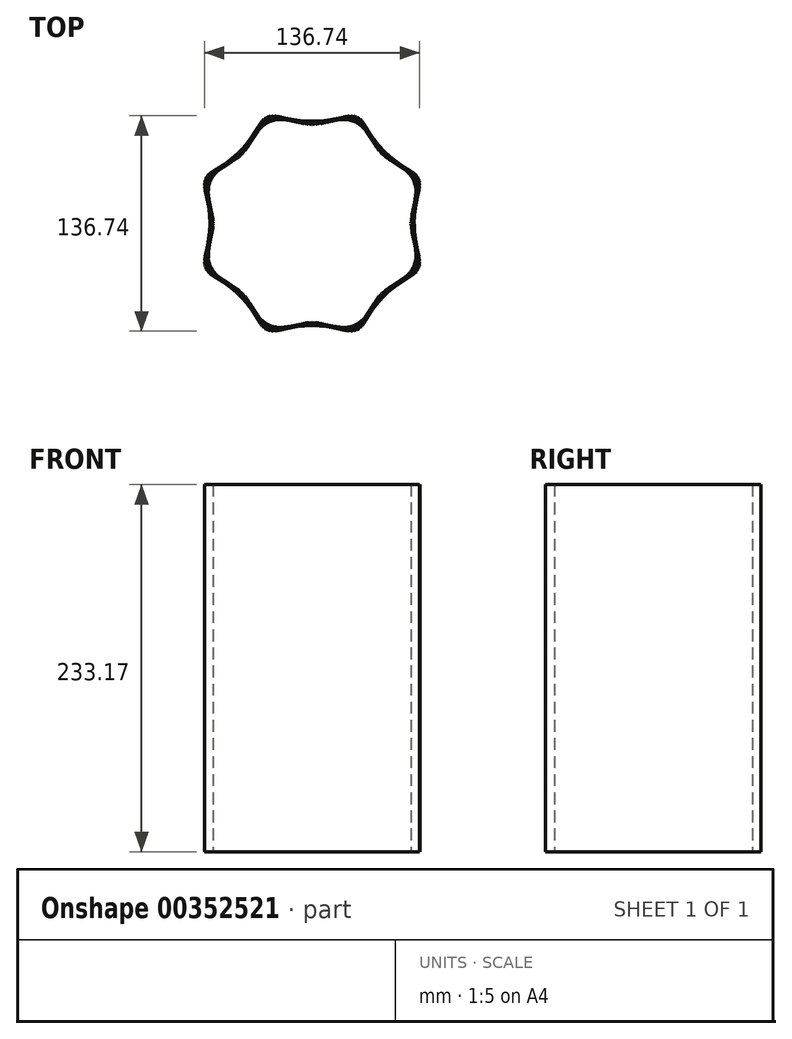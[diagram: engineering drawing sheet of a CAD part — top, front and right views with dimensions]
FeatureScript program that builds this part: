
annotation { "Feature Type Name" : "Feature", "Feature Type Description" : "" }
export const myFeature = defineFeature(function(context is Context, id is Id, definition is map)
    precondition{}
    {
        {
            var Q0;
            Q0=qCreatedBy(makeId("Top.planeOp"),FACE);
            var sketch = newSketch(context, id + "F0", { "sketchPlane" : qUnion([Q0])});
            skLineSegment(sketch, "E0", {"start": v(0, 0) * mm, "end": v(0, 62.86) * mm});
            skLineSegment(sketch, "E1.1.0", {"start": v(0, 0) * mm, "end": v(-44.45, 44.45) * mm});
            skLineSegment(sketch, "E1.2.0", {"start": v(0, 0) * mm, "end": v(-62.86, 0) * mm});
            skLineSegment(sketch, "E1.3.0", {"start": v(0, 0) * mm, "end": v(-44.45, -44.45) * mm});
            skLineSegment(sketch, "E1.4.0", {"start": v(0, 0) * mm, "end": v(0, -62.86) * mm});
            skLineSegment(sketch, "E1.5.0", {"start": v(0, 0) * mm, "end": v(44.45, -44.45) * mm});
            skLineSegment(sketch, "E1.6.0", {"start": v(0, 0) * mm, "end": v(62.86, 0) * mm});
            skLineSegment(sketch, "E1.7.0", {"start": v(0, 0) * mm, "end": v(44.45, 44.45) * mm});
            skPoint(sketch, "E1.center", {"position": v(0, 0) * mm});
            skSolve(sketch);
        }
        {
            var Q0;
            Q0=qCreatedBy(makeId("Top.planeOp"),FACE);
            var sketch = newSketch(context, id + "F1", { "sketchPlane" : qUnion([Q0])});
            skLineSegment(sketch, "E2", {"start": v(0, 0) * mm, "end": v(40.7, 0) * mm});
            skLineSegment(sketch, "E3.1.0", {"start": v(0, 0) * mm, "end": v(37.6, 15.58) * mm});
            skLineSegment(sketch, "E3.2.0", {"start": v(0, 0) * mm, "end": v(28.78, 28.78) * mm});
            skLineSegment(sketch, "E3.3.0", {"start": v(0, 0) * mm, "end": v(15.58, 37.6) * mm});
            skLineSegment(sketch, "E3.4.0", {"start": v(0, 0) * mm, "end": v(0, 40.7) * mm});
            skLineSegment(sketch, "E3.5.0", {"start": v(0, 0) * mm, "end": v(-15.58, 37.6) * mm});
            skLineSegment(sketch, "E3.6.0", {"start": v(0, 0) * mm, "end": v(-28.78, 28.78) * mm});
            skLineSegment(sketch, "E3.7.0", {"start": v(0, 0) * mm, "end": v(-37.6, 15.58) * mm});
            skLineSegment(sketch, "E3.8.0", {"start": v(0, 0) * mm, "end": v(-40.7, 0) * mm});
            skLineSegment(sketch, "E3.9.0", {"start": v(0, 0) * mm, "end": v(-37.6, -15.58) * mm});
            skLineSegment(sketch, "E3.10.0", {"start": v(0, 0) * mm, "end": v(-28.78, -28.78) * mm});
            skLineSegment(sketch, "E3.11.0", {"start": v(0, 0) * mm, "end": v(-15.58, -37.6) * mm});
            skLineSegment(sketch, "E3.12.0", {"start": v(0, 0) * mm, "end": v(0, -40.7) * mm});
            skLineSegment(sketch, "E3.13.0", {"start": v(0, 0) * mm, "end": v(15.58, -37.6) * mm});
            skLineSegment(sketch, "E3.14.0", {"start": v(0, 0) * mm, "end": v(28.78, -28.78) * mm});
            skLineSegment(sketch, "E3.15.0", {"start": v(0, 0) * mm, "end": v(37.6, -15.58) * mm});
            skPoint(sketch, "E3.center", {"position": v(0, 0) * mm});
            skSolve(sketch);
        }
        {
            var Q0;
            Q0=qCreatedBy(makeId("Top.planeOp"),FACE);
            cPlane(context, id + "F2", {"entities" : qUnion([Q0]), "cplaneType" : CPlaneType.OFFSET, "offset" : 110.49 * mm, "oppositeDirection" : true, "width" : 152.4 * mm, "height" : 152.4 * mm});
        }
        {
            var Q0;
            Q0=qCreatedBy(id+"F2.planeOp",FACE);
            var sketch = newSketch(context, id + "F3", { "sketchPlane" : qUnion([Q0])});
            skLineSegment(sketch, "E4", {"start": v(0, 0) * mm, "end": v(0, 62.86) * mm});
            skLineSegment(sketch, "E5.1.0", {"start": v(0, 0) * mm, "end": v(-44.45, 44.45) * mm});
            skLineSegment(sketch, "E5.2.0", {"start": v(0, 0) * mm, "end": v(-62.86, 0) * mm});
            skLineSegment(sketch, "E5.3.0", {"start": v(0, 0) * mm, "end": v(-44.45, -44.45) * mm});
            skLineSegment(sketch, "E5.4.0", {"start": v(0, 0) * mm, "end": v(0, -62.86) * mm});
            skLineSegment(sketch, "E5.5.0", {"start": v(0, 0) * mm, "end": v(44.45, -44.45) * mm});
            skLineSegment(sketch, "E5.6.0", {"start": v(0, 0) * mm, "end": v(62.86, 0) * mm});
            skLineSegment(sketch, "E5.7.0", {"start": v(0, 0) * mm, "end": v(44.45, 44.45) * mm});
            skPoint(sketch, "E5.center", {"position": v(0, 0) * mm});
            skSolve(sketch);
        }
        {
            var Q0;
            Q0=qCreatedBy(id+"F2.planeOp",FACE);
            var sketch = newSketch(context, id + "F4", { "sketchPlane" : qUnion([Q0])});
            skLineSegment(sketch, "E6", {"start": v(0, 0) * mm, "end": v(0, 73.37) * mm});
            skLineSegment(sketch, "E7.1.0", {"start": v(0, 0) * mm, "end": v(-28.08, 67.79) * mm});
            skLineSegment(sketch, "E7.2.0", {"start": v(0, 0) * mm, "end": v(-51.88, 51.88) * mm});
            skLineSegment(sketch, "E7.3.0", {"start": v(0, 0) * mm, "end": v(-67.79, 28.08) * mm});
            skLineSegment(sketch, "E7.4.0", {"start": v(0, 0) * mm, "end": v(-73.37, 0) * mm});
            skLineSegment(sketch, "E7.5.0", {"start": v(0, 0) * mm, "end": v(-67.79, -28.08) * mm});
            skLineSegment(sketch, "E7.6.0", {"start": v(0, 0) * mm, "end": v(-51.88, -51.88) * mm});
            skLineSegment(sketch, "E7.7.0", {"start": v(0, 0) * mm, "end": v(-28.08, -67.79) * mm});
            skLineSegment(sketch, "E7.8.0", {"start": v(0, 0) * mm, "end": v(0, -73.37) * mm});
            skLineSegment(sketch, "E7.9.0", {"start": v(0, 0) * mm, "end": v(28.08, -67.79) * mm});
            skLineSegment(sketch, "E7.10.0", {"start": v(0, 0) * mm, "end": v(51.88, -51.88) * mm});
            skLineSegment(sketch, "E7.11.0", {"start": v(0, 0) * mm, "end": v(67.79, -28.08) * mm});
            skLineSegment(sketch, "E7.12.0", {"start": v(0, 0) * mm, "end": v(73.37, 0) * mm});
            skLineSegment(sketch, "E7.13.0", {"start": v(0, 0) * mm, "end": v(67.79, 28.08) * mm});
            skLineSegment(sketch, "E7.14.0", {"start": v(0, 0) * mm, "end": v(51.88, 51.88) * mm});
            skLineSegment(sketch, "E7.15.0", {"start": v(0, 0) * mm, "end": v(28.08, 67.79) * mm});
            skPoint(sketch, "E7.center", {"position": v(0, 0) * mm});
            skSolve(sketch);
        }
        {
            var Q0;
            Q0=qCreatedBy(id+"F2.planeOp",FACE);
            cPlane(context, id + "F5", {"entities" : qUnion([Q0]), "cplaneType" : CPlaneType.OFFSET, "offset" : 63 * mm, "oppositeDirection" : true, "width" : 152.4 * mm, "height" : 152.4 * mm});
        }
        {
            var Q0;
            Q0=qCreatedBy(id+"F5.planeOp",FACE);
            var sketch = newSketch(context, id + "F6", { "sketchPlane" : qUnion([Q0])});
            skLineSegment(sketch, "E8", {"start": v(0, 0) * mm, "end": v(0, 62.86) * mm});
            skLineSegment(sketch, "E9.1.0", {"start": v(0, 0) * mm, "end": v(-44.45, 44.45) * mm});
            skLineSegment(sketch, "E9.2.0", {"start": v(0, 0) * mm, "end": v(-62.86, 0) * mm});
            skLineSegment(sketch, "E9.3.0", {"start": v(0, 0) * mm, "end": v(-44.45, -44.45) * mm});
            skLineSegment(sketch, "E9.4.0", {"start": v(0, 0) * mm, "end": v(0, -62.86) * mm});
            skLineSegment(sketch, "E9.5.0", {"start": v(0, 0) * mm, "end": v(44.45, -44.45) * mm});
            skLineSegment(sketch, "E9.6.0", {"start": v(0, 0) * mm, "end": v(62.86, 0) * mm});
            skLineSegment(sketch, "E9.7.0", {"start": v(0, 0) * mm, "end": v(44.45, 44.45) * mm});
            skPoint(sketch, "E9.center", {"position": v(0, 0) * mm});
            skFitSpline(sketch, "E10", {"points": [v(0, 62.86) * mm, v(28.08, 67.79) * mm, v(44.46, 44.45) * mm, v(67.8, 28.08) * mm, v(62.87, 0) * mm, v(67.77, -28.07) * mm, v(44.46, -44.45) * mm, v(28.08, -67.8) * mm, v(0, -62.87) * mm, v(-28.07, -67.8) * mm, v(-44.45, -44.45) * mm, v(-67.78, -28.08) * mm, v(-62.86, 0) * mm, v(-67.78, 28.08) * mm, v(-44.45, 44.45) * mm, v(-28.07, 67.79) * mm, v(0, 62.86) * mm]});
            skSolve(sketch);
        }
        {
            var Q0;
            Q0=qCreatedBy(id+"F2.planeOp",FACE);
            cPlane(context, id + "F7", {"entities" : qUnion([Q0]), "cplaneType" : CPlaneType.OFFSET, "offset" : 170.18 * mm, "width" : 152.4 * mm, "height" : 152.4 * mm});
        }
        {
            var Q0;
            Q0=qCreatedBy(id+"F7.planeOp",FACE);
            var sketch = newSketch(context, id + "F8", { "sketchPlane" : qUnion([Q0])});
            skFitSpline(sketch, "E11", {"points": [v(0, 62.86) * mm, v(28.08, 67.79) * mm, v(44.46, 44.45) * mm, v(67.8, 28.08) * mm, v(62.87, 0) * mm, v(67.77, -28.07) * mm, v(44.46, -44.45) * mm, v(28.08, -67.8) * mm, v(0, -62.87) * mm, v(-28.07, -67.8) * mm, v(-44.45, -44.45) * mm, v(-67.78, -28.08) * mm, v(-62.86, 0) * mm, v(-67.78, 28.08) * mm, v(-44.45, 44.45) * mm, v(-28.07, 67.79) * mm, v(0, 62.86) * mm]});
            skLineSegment(sketch, "E12", {"start": v(0, 0) * mm, "end": v(0, 62.86) * mm});
            skLineSegment(sketch, "E13.1.0", {"start": v(0, 0) * mm, "end": v(-44.45, 44.45) * mm});
            skLineSegment(sketch, "E13.2.0", {"start": v(0, 0) * mm, "end": v(-62.86, 0) * mm});
            skLineSegment(sketch, "E13.3.0", {"start": v(0, 0) * mm, "end": v(-44.45, -44.45) * mm});
            skLineSegment(sketch, "E13.4.0", {"start": v(0, 0) * mm, "end": v(0, -62.86) * mm});
            skLineSegment(sketch, "E13.5.0", {"start": v(0, 0) * mm, "end": v(44.45, -44.45) * mm});
            skLineSegment(sketch, "E13.6.0", {"start": v(0, 0) * mm, "end": v(62.86, 0) * mm});
            skLineSegment(sketch, "E13.7.0", {"start": v(0, 0) * mm, "end": v(44.45, 44.45) * mm});
            skPoint(sketch, "E13.center", {"position": v(0, 0) * mm});
            skSolve(sketch);
        }
        {
            var Q0;
            {var subQ3=sQuery(id+"F6.wireOp",EDGE,"E10");Q0=makeQuery(id+"F6.imprint","IMPRINT",FACE,{"disambiguationData":[TD([[makeQuery(id+"F6.imprint","IMPRINT",EDGE,{"derivedFrom":subQ3}),-1.0]])]});}
            var Q1;
            {var subQ0=sQuery(id+"F8.wireOp",EDGE,"E11");Q1=makeQuery(id+"F8.imprint","IMPRINT",FACE,{"disambiguationData":[TD([[makeQuery(id+"F8.imprint","IMPRINT",EDGE,{"derivedFrom":subQ0}),-1.0]])]});}
            var Q2;
            Q2=sQuery(id+"F6.wireOp",EDGE,"E10");
            var Q3;
            Q3=sQuery(id+"F8.wireOp",EDGE,"E11");
            loft(context, id + "F9", {"bodyType" : ToolBodyType.SURFACE, "sheetProfilesArray" : [{ "sheetProfileEntities" : qUnion([Q0]) }, { "sheetProfileEntities" : qUnion([Q1]) }], "wireProfilesArray" : [{ "wireProfileEntities" : qUnion([Q2]) }, { "wireProfileEntities" : qUnion([Q3]) }]});
        }
        {
            var Q0;
            Q0=qCreatedBy(makeId("Front.planeOp"),FACE);
            var sketch = newSketch(context, id + "F10", { "sketchPlane" : qUnion([Q0])});
            skLineSegment(sketch, "E14", {"start": v(0, -110.79) * mm, "end": v(0, 0) * mm});
            skSolve(sketch);
        }
        {
            var Q0;
            Q0=makeQuery(id+"F9.opLoft","SWEPT_BODY",BODY,{"disambiguationData":[OSD([sQuery(id+"F6.wireOp",EDGE,"E10"),sQuery(id+"F8.wireOp",EDGE,"E11")])]});
            var Q1;
            Q1=sQuery(id+"F10.wireOp",EDGE,"E14");
            circularPattern(context, id + "F11", {"entities" : qUnion([Q0]), "axis" : qUnion([Q1]), "angle" : 360 * degree, "instanceCount" : 8, "equalSpace" : true});
        }
    });
